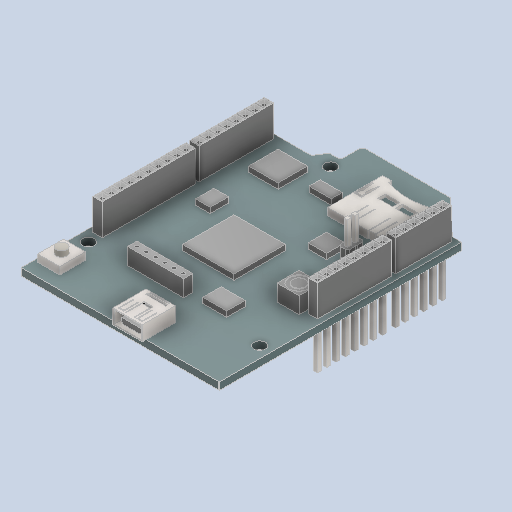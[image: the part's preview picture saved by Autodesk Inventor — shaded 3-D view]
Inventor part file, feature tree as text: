
AUTODESK INVENTOR PART (.ipt)
format: ipt  version: 2024 (Build 280153000, 153)  size: 584,192 bytes
history: native  units: in
note: dims shown in document units (in); Inventor stores cm internally (conversion verified against a paired STEP export)
features: other x5, fillet x1
ambient origin geometry x8: Origin, YZ Plane, XZ Plane, XY Plane, X Axis, Y Axis, Z Axis, Center Point
bodies: Solid1 (feature_tree)
feature tree (6):
  other  "Droite"
  other  "Plaque"
  other  "Arriere"
  other  "Platine"
  other  "Borne"
  fillet  "Congé1"  [1 undecoded]
note: 1 required parameter value undecoded (feature->parameter linkage not recoverable at this tier; creation-order binding heuristic only, values carry confidence <= 0.55)
